# Revit family: Open Fronted Modular Storage With Glass Door Options
name_source: partatom
category: Furniture
units: mm (PartAtom-declared; Revit-internal decimal feet)

## family parameters
Always vertical = Yes
Cut with Voids When Loaded = No
OmniClass Number = 23.40.20.00
OmniClass Title = General Furniture and Specialties
Room Calculation Point = No
Shared = No
Work Plane-Based = No

## types (3) — shared parameters
BOF10Z Shelves = Yes
Carcass = Gresham - MIDNIGHT ASH VERTICAL
Depth = 400 mm  [stored 1.31234 ft]
Doors = Gresham - PLUM
Manufacturer = Gresham Office Furniture
Model = BOOKCASE
Range = STORAGE
Shelves = Gresham - MIDNIGHT ASH
URL = www.gof.co.uk
Width = 1200 mm  [stored 3.93701 ft]

## per-type parameters (varying)
| type | BOF14Z Shelves | BOF18Z Shelves | Height |
| BOF18Z | Yes | Yes | 1816 mm  [stored 5.95801 ft] |
| BOF14Z | Yes | No | 1400 mm  [stored 4.59318 ft] |
| BOF10Z | No | No | 985 mm  [stored 3.23163 ft] |

note: column(s) folded — value = type name in every type: Product Code

note: [stored X ft] marks values corroborated as IEEE doubles in the binary element streams (Revit-internal decimal feet)

## geometry (parser evidence)
native form markers: Sweep x69
no freeform markers — native parametric forms only
